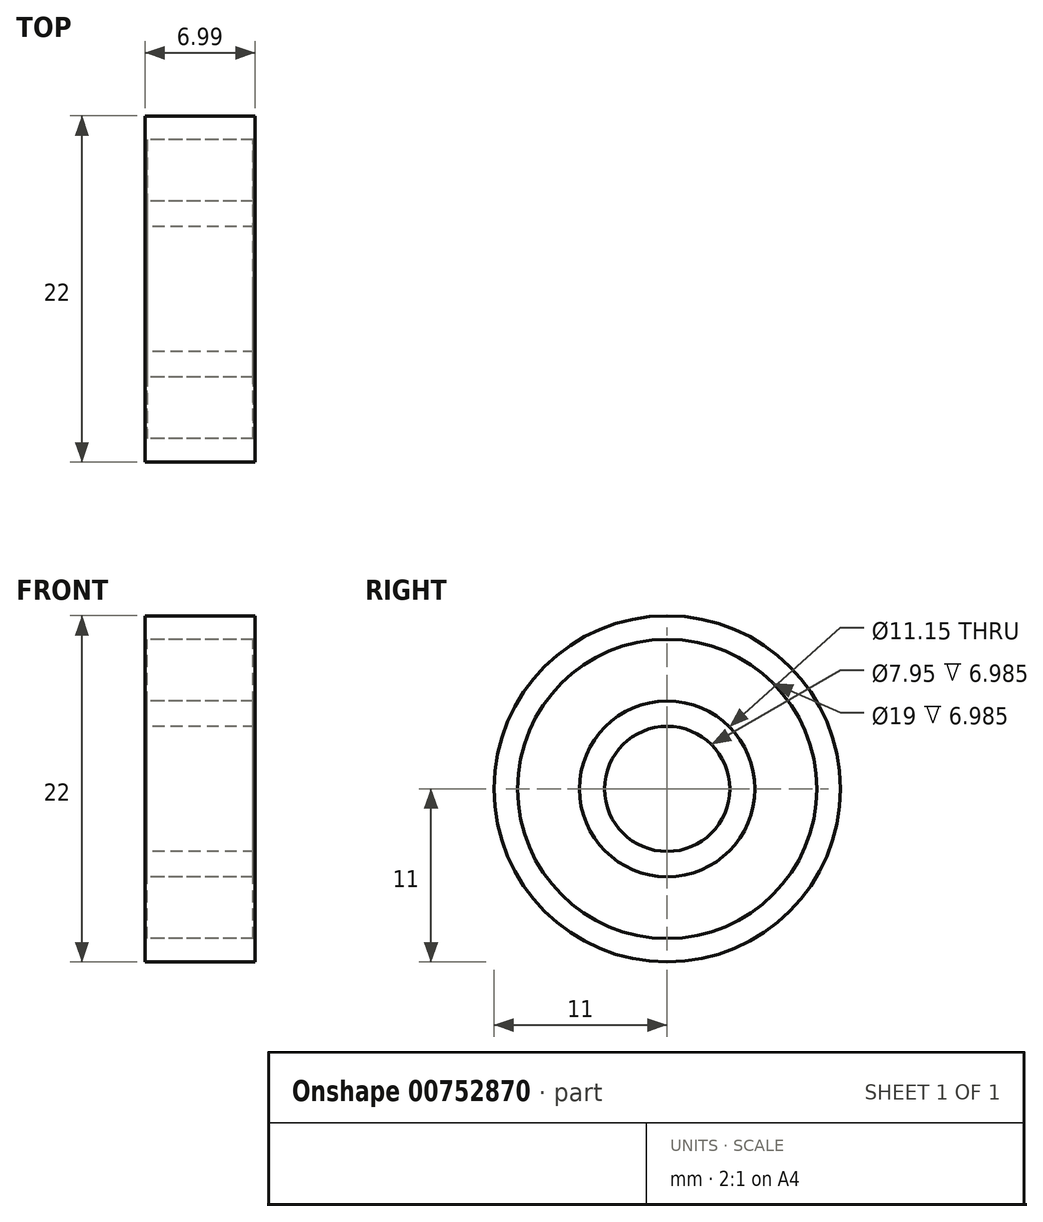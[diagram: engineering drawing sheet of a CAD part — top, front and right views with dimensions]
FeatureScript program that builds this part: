
annotation { "Feature Type Name" : "Feature", "Feature Type Description" : "" }
export const myFeature = defineFeature(function(context is Context, id is Id, definition is map)
    precondition{}
    {
        {
            var Q0;
            Q0=qCreatedBy(makeId("Right.planeOp"),FACE);
            var sketch = newSketch(context, id + "F0", { "sketchPlane" : qUnion([Q0])});
            skCircle(sketch, "E0", {"center": v(0, 0) * mm, "radius": 3.98 * mm});
            skCircle(sketch, "E1", {"center": v(0, 0) * mm, "radius": 5.58 * mm});
            skCircle(sketch, "E2", {"center": v(0, 0) * mm, "radius": 9.5 * mm});
            skCircle(sketch, "E3", {"center": v(0, 0) * mm, "radius": 11 * mm});
            skSolve(sketch);
        }
        {
            var Q0;
            Q0=makeQuery(id+"F0.imprint","IMPRINT",FACE,{"disambiguationData":[TD([[makeQuery(id+"F0.imprint","IMPRINT",EDGE,{"derivedFrom":sQuery(id+"F0.wireOp",EDGE,"E0")}),-1.0]])]});
            var Q1;
            Q1=makeQuery(id+"F0.imprint","IMPRINT",FACE,{"disambiguationData":[TD([[makeQuery(id+"F0.imprint","IMPRINT",EDGE,{"derivedFrom":sQuery(id+"F0.wireOp",EDGE,"E2")}),-1.0]])]});
            extrude(context, id + "F1", {"entities" : qUnion([Q0, Q1]), "depth" : 7 * mm, "offsetDistance" : 25.4 * mm});
        }
        {
            var Q0;
            Q0=makeQuery(id+"F0.imprint","IMPRINT",FACE,{"disambiguationData":[TD([[makeQuery(id+"F0.imprint","IMPRINT",EDGE,{"derivedFrom":sQuery(id+"F0.wireOp",EDGE,"E1")}),-1.0]])]});
            extrude(context, id + "F2", {"entities" : qUnion([Q0]), "depth" : 6.86 * mm, "offsetDistance" : 25.4 * mm, "hasSecondDirection" : true, "secondDirectionOppositeDirection" : false, "secondDirectionDepth" : 0.13 * mm});
        }
    });
